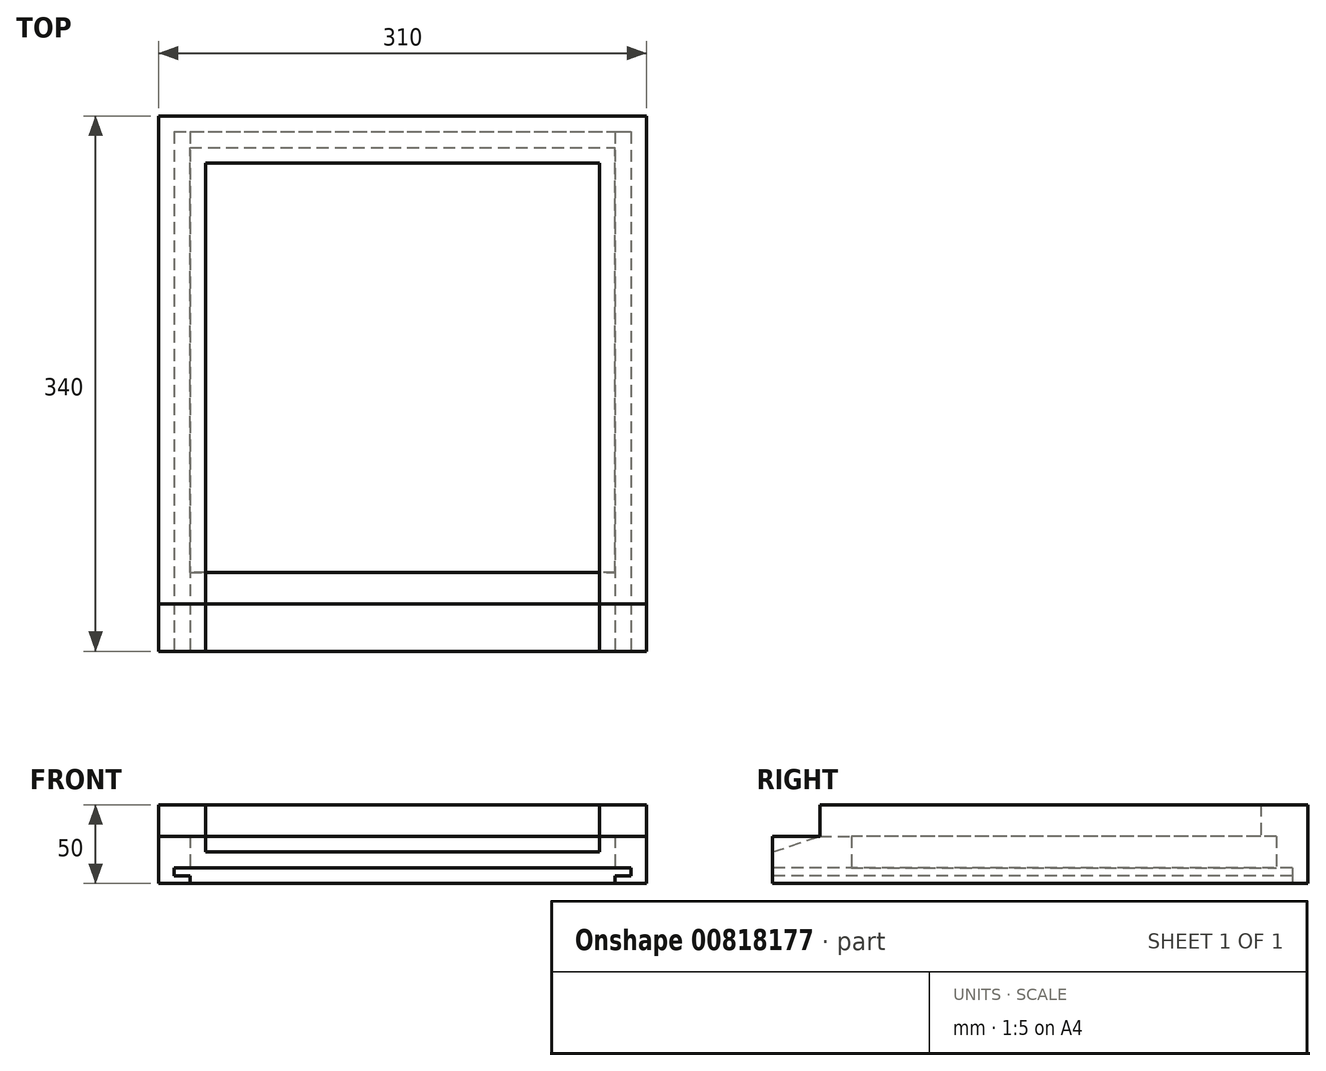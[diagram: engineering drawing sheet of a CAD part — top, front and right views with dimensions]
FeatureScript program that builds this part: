
annotation { "Feature Type Name" : "Feature", "Feature Type Description" : "" }
export const myFeature = defineFeature(function(context is Context, id is Id, definition is map)
    precondition{}
    {
        {
            var Q0;
            Q0=qCreatedBy(makeId("Top.planeOp"),FACE);
            var sketch = newSketch(context, id + "F0", { "sketchPlane" : qUnion([Q0])});
            skLineSegment(sketch, "E0.bottom", {"start": v(155, -155) * mm, "end": v(-155, -155) * mm});
            skLineSegment(sketch, "E0.top", {"start": v(155, 155) * mm, "end": v(-155, 155) * mm});
            skLineSegment(sketch, "E0.left", {"start": v(155, -155) * mm, "end": v(155, 155) * mm});
            skLineSegment(sketch, "E0.right", {"start": v(-155, -155) * mm, "end": v(-155, 155) * mm});
            skPoint(sketch, "E0.middle", {"position": v(0, 0) * mm});
            skLineSegment(sketch, "E1.bottom", {"start": v(-155, -155) * mm, "end": v(155, -155) * mm});
            skLineSegment(sketch, "E1.top", {"start": v(-155, -185) * mm, "end": v(155, -185) * mm});
            skLineSegment(sketch, "E1.left", {"start": v(-155, -155) * mm, "end": v(-155, -185) * mm});
            skLineSegment(sketch, "E1.right", {"start": v(155, -155) * mm, "end": v(155, -185) * mm});
            skLineSegment(sketch, "E2.bottom", {"start": v(125, -125) * mm, "end": v(-125, -125) * mm});
            skLineSegment(sketch, "E2.top", {"start": v(125, 125) * mm, "end": v(-125, 125) * mm});
            skLineSegment(sketch, "E2.left", {"start": v(125, -125) * mm, "end": v(125, 125) * mm});
            skLineSegment(sketch, "E2.right", {"start": v(-125, -125) * mm, "end": v(-125, 125) * mm});
            skLineSegment(sketch, "E3", {"start": v(-125, -125) * mm, "end": v(-125, -155) * mm});
            skLineSegment(sketch, "E4", {"start": v(125, -125) * mm, "end": v(125, -155) * mm});
            skSolve(sketch);
        }
        {
            var Q0;
            Q0=makeQuery(id+"F0.imprint","IMPRINT",FACE,{"disambiguationData":[TD([[makeQuery(id+"F0.imprint","IMPRINT",EDGE,{"derivedFrom":sQuery(id+"F0.wireOp",EDGE,"E0.top")}),1.0]])]});
            extrude(context, id + "F1", {"entities" : qUnion([Q0]), "depth" : 30 * mm, "offsetDistance" : 25 * mm});
        }
        {
            var Q0;
            Q0 = qSketchRegion(id + "F0", true);
            extrude(context, id + "F2", {"entities" : qUnion([Q0]), "operationType" : NewBodyOperationType.ADD, "depth" : 10 * mm, "offsetDistance" : 25 * mm});
        }
        {
            var Q0;
            Q0=makeQuery(id+"F0.imprint","IMPRINT",FACE,{"disambiguationData":[TD([[makeQuery(id+"F0.imprint","IMPRINT",EDGE,{"derivedFrom":sQuery(id+"F0.wireOp",EDGE,"E2.bottom")}),-1.0]])]});
            var Q1;
            Q1=makeQuery(id+"F0.imprint","IMPRINT",FACE,{"disambiguationData":[TD([[makeQuery(id+"F0.imprint","IMPRINT",EDGE,{"derivedFrom":sQuery(id+"F0.wireOp",EDGE,"E0.top")}),1.0]])]});
            var Q2;
            Q2=makeQuery(id+"F0.imprint","IMPRINT",FACE,{"disambiguationData":[TD([[makeQuery(id+"F0.imprint","IMPRINT",EDGE,{"derivedFrom":sQuery(id+"F0.wireOp",EDGE,"E1.top")}),1.0]])]});
            var Q3;
            Q3=makeQuery(id+"F0.imprint","IMPRINT",FACE,{"disambiguationData":[TD([[makeQuery(id+"F0.imprint","IMPRINT",EDGE,{"derivedFrom":sQuery(id+"F0.wireOp",EDGE,"E2.bottom")}),1.0]])]});
            extrude(context, id + "F3", {"entities" : qUnion([Q0, Q1, Q2, Q3]), "operationType" : NewBodyOperationType.ADD, "depth" : 10 * mm, "offsetDistance" : 25 * mm});
        }
        {
            var Q0;
            {var subQ0=sQuery(id+"F0.wireOp",EDGE,"E0.right");Q0=makeQuery(id+"F2.boolean.opBoolean","MERGE",FACE,{"derivedFrom":[makeQuery(id+"F1.opExtrude","SWEPT_FACE",FACE,{"disambiguationData":[OSD([subQ0])]}),makeQuery(id+"F2.opExtrude","SWEPT_FACE",FACE,{"disambiguationData":[OSD([subQ0,sQuery(id+"F0.wireOp",EDGE,"E1.left")])]})]});}
            cPlane(context, id + "F4", {"entities" : qUnion([Q0]), "cplaneType" : CPlaneType.OFFSET, "offset" : 30 * mm, "oppositeDirection" : true, "width" : 150 * mm, "height" : 150 * mm});
        }
        {
            var Q0;
            Q0=qCreatedBy(id+"F4.planeOp",FACE);
            var sketch = newSketch(context, id + "F5", { "sketchPlane" : qUnion([Q0])});
            skLineSegment(sketch, "E5", {"start": v(185, 0) * mm, "end": v(155, 10) * mm});
            skLineSegment(sketch, "E6", {"start": v(155, 10) * mm, "end": v(185, 10) * mm});
            skLineSegment(sketch, "E7", {"start": v(185, 10) * mm, "end": v(185, 0) * mm});
            skSolve(sketch);
        }
        {
            var Q0;
            Q0 = qSketchRegion(id + "F5", true);
            extrude(context, id + "F6", {"entities" : qUnion([Q0]), "operationType" : NewBodyOperationType.REMOVE, "oppositeDirection" : true, "depth" : 250 * mm, "offsetDistance" : 25 * mm});
        }
        {
            var Q0;
            {var subQ0=sQuery(id+"F0.wireOp",EDGE,"E1.right");var subQ1=sQuery(id+"F0.wireOp",EDGE,"E1.left");var subQ2=sQuery(id+"F0.wireOp",EDGE,"E1.top");var subQ3=sQuery(id+"F0.wireOp",EDGE,"E0.right");var subQ4=sQuery(id+"F0.wireOp",EDGE,"E0.left");var subQ5=sQuery(id+"F0.wireOp",EDGE,"E0.top");var subQ6=sQuery(id+"F0.wireOp",EDGE,"E4");var subQ7=sQuery(id+"F0.wireOp",EDGE,"E3");var subQ8=sQuery(id+"F0.wireOp",EDGE,"E2.right");var subQ9=sQuery(id+"F0.wireOp",EDGE,"E2.left");var subQ10=sQuery(id+"F0.wireOp",EDGE,"E2.top");var subQ11=sQuery(id+"F0.wireOp",EDGE,"E1.bottom");Q0=makeQuery(id+"F3.boolean.opBoolean","MERGE",FACE,{"derivedFrom":[makeQuery(id+"F2.boolean.opBoolean","MERGE",FACE,{"derivedFrom":[makeQuery(id+"F1.opExtrude","CAP_FACE",FACE,{"disambiguationData":[OSD([subQ5,subQ4,subQ3,subQ11,subQ10,subQ9,subQ8,subQ7,subQ6])],"isStart":true}),makeQuery(id+"F2.opExtrude","CAP_FACE",FACE,{"disambiguationData":[OSD([subQ5,subQ4,subQ3,subQ11,subQ2,subQ1,subQ0,subQ10,subQ9,subQ8,subQ7,subQ6])],"isStart":true})]}),makeQuery(id+"F3.opExtrude","CAP_FACE",FACE,{"disambiguationData":[OSD([subQ5,subQ4,subQ3,subQ2,subQ1,subQ0])],"isStart":true})]});}
            var sketch = newSketch(context, id + "F7", { "sketchPlane" : qUnion([Q0])});
            skLineSegment(sketch, "E8.bottom", {"start": v(135, -135) * mm, "end": v(-135, -135) * mm});
            skLineSegment(sketch, "E8.top", {"start": v(135, 135) * mm, "end": v(-135, 135) * mm});
            skLineSegment(sketch, "E8.left", {"start": v(135, -135) * mm, "end": v(135, 135) * mm});
            skLineSegment(sketch, "E8.right", {"start": v(-135, -135) * mm, "end": v(-135, 135) * mm});
            skPoint(sketch, "E8.middle", {"position": v(0, 0) * mm});
            skSolve(sketch);
        }
        {
            var Q0;
            Q0 = qSketchRegion(id + "F7", true);
            extrude(context, id + "F8", {"entities" : qUnion([Q0]), "operationType" : NewBodyOperationType.REMOVE, "oppositeDirection" : true, "depth" : 10 * mm, "offsetDistance" : 25 * mm});
        }
        {
            var Q0;
            {var subQ0=sQuery(id+"F0.wireOp",EDGE,"E1.right");var subQ1=sQuery(id+"F0.wireOp",EDGE,"E1.left");var subQ2=sQuery(id+"F0.wireOp",EDGE,"E1.top");var subQ3=sQuery(id+"F0.wireOp",EDGE,"E0.right");var subQ4=sQuery(id+"F0.wireOp",EDGE,"E0.left");var subQ5=sQuery(id+"F0.wireOp",EDGE,"E0.top");var subQ6=sQuery(id+"F0.wireOp",EDGE,"E4");var subQ7=sQuery(id+"F0.wireOp",EDGE,"E3");var subQ8=sQuery(id+"F0.wireOp",EDGE,"E2.right");var subQ9=sQuery(id+"F0.wireOp",EDGE,"E2.left");var subQ10=sQuery(id+"F0.wireOp",EDGE,"E2.top");var subQ11=sQuery(id+"F0.wireOp",EDGE,"E1.bottom");Q0=makeQuery(id+"F3.boolean.opBoolean","MERGE",FACE,{"derivedFrom":[makeQuery(id+"F2.boolean.opBoolean","MERGE",FACE,{"derivedFrom":[makeQuery(id+"F1.opExtrude","CAP_FACE",FACE,{"disambiguationData":[OSD([subQ5,subQ4,subQ3,subQ11,subQ10,subQ9,subQ8,subQ7,subQ6])],"isStart":true}),makeQuery(id+"F2.opExtrude","CAP_FACE",FACE,{"disambiguationData":[OSD([subQ5,subQ4,subQ3,subQ11,subQ2,subQ1,subQ0,subQ10,subQ9,subQ8,subQ7,subQ6])],"isStart":true})]}),makeQuery(id+"F3.opExtrude","CAP_FACE",FACE,{"disambiguationData":[OSD([subQ5,subQ4,subQ3,subQ2,subQ1,subQ0])],"isStart":true})]});}
            extrude(context, id + "F9", {"entities" : qUnion([Q0]), "operationType" : NewBodyOperationType.ADD, "depth" : 20 * mm, "offsetDistance" : 25 * mm});
        }
        {
            var Q0;
            {var subQ0=sQuery(id+"F5.wireOp",EDGE,"E7");var subQ1=sQuery(id+"F5.wireOp",EDGE,"E5");var subQ2=sQuery(id+"F0.wireOp",EDGE,"E1.top");var subQ11=sQuery(id+"F0.wireOp",EDGE,"E0.right");var subQ12=sQuery(id+"F0.wireOp",EDGE,"E0.left");var subQ21=makeQuery(id+"F2.opExtrude","SWEPT_FACE",FACE,{"disambiguationData":[OSD([subQ2])]});Q0=makeQuery(id+"F9.boolean.opBoolean","MERGE",FACE,{"derivedFrom":[makeQuery(id+"F6.boolean.opBoolean","SPLIT",FACE,{"disambiguationData":[TD([makeQuery(id+"F1.opExtrude","SWEPT_FACE",FACE,{"disambiguationData":[OSD([subQ11])]})])],"derivedFrom":subQ21}),makeQuery(id+"F6.boolean.opBoolean","SPLIT",FACE,{"disambiguationData":[TD([makeQuery(id+"F1.opExtrude","SWEPT_FACE",FACE,{"disambiguationData":[OSD([subQ12])]})])],"derivedFrom":subQ21}),makeQuery(id+"F9.opExtrude","SWEPT_FACE",FACE,{"disambiguationData":[OSD([subQ2,subQ1,subQ0])]})]});}
            var sketch = newSketch(context, id + "F10", { "sketchPlane" : qUnion([Q0])});
            skLineSegment(sketch, "E9.bottom", {"start": v(-145, -10) * mm, "end": v(145, -10) * mm});
            skLineSegment(sketch, "E9.top", {"start": v(-145, -15) * mm, "end": v(145, -15) * mm});
            skLineSegment(sketch, "E9.left", {"start": v(-145, -10) * mm, "end": v(-145, -15) * mm});
            skLineSegment(sketch, "E9.right", {"start": v(145, -10) * mm, "end": v(145, -15) * mm});
            skLineSegment(sketch, "E10", {"start": v(-135, -15) * mm, "end": v(-135, -20) * mm});
            skLineSegment(sketch, "E11", {"start": v(135, -15) * mm, "end": v(135, -20) * mm});
            skLineSegment(sketch, "E12", {"start": v(-135, -20) * mm, "end": v(135, -20) * mm});
            skSolve(sketch);
        }
        {
            var Q0;
            Q0=makeQuery(id+"F10.imprint","IMPRINT",FACE,{"disambiguationData":[TD([[makeQuery(id+"F10.imprint","IMPRINT",EDGE,{"derivedFrom":sQuery(id+"F10.wireOp",EDGE,"E9.bottom")}),-1.0]])]});
            var Q1;
            {var subQ0=sQuery(id+"F10.wireOp",EDGE,"E10");Q1=makeQuery(id+"F10.imprint","IMPRINT",FACE,{"disambiguationData":[TD([[makeQuery(id+"F10.imprint","IMPRINT",EDGE,{"derivedFrom":subQ0}),1.0]])]});}
            extrude(context, id + "F11", {"entities" : qUnion([Q0, Q1]), "operationType" : NewBodyOperationType.REMOVE, "oppositeDirection" : true, "depth" : 330 * mm, "offsetDistance" : 25 * mm});
        }
    });
